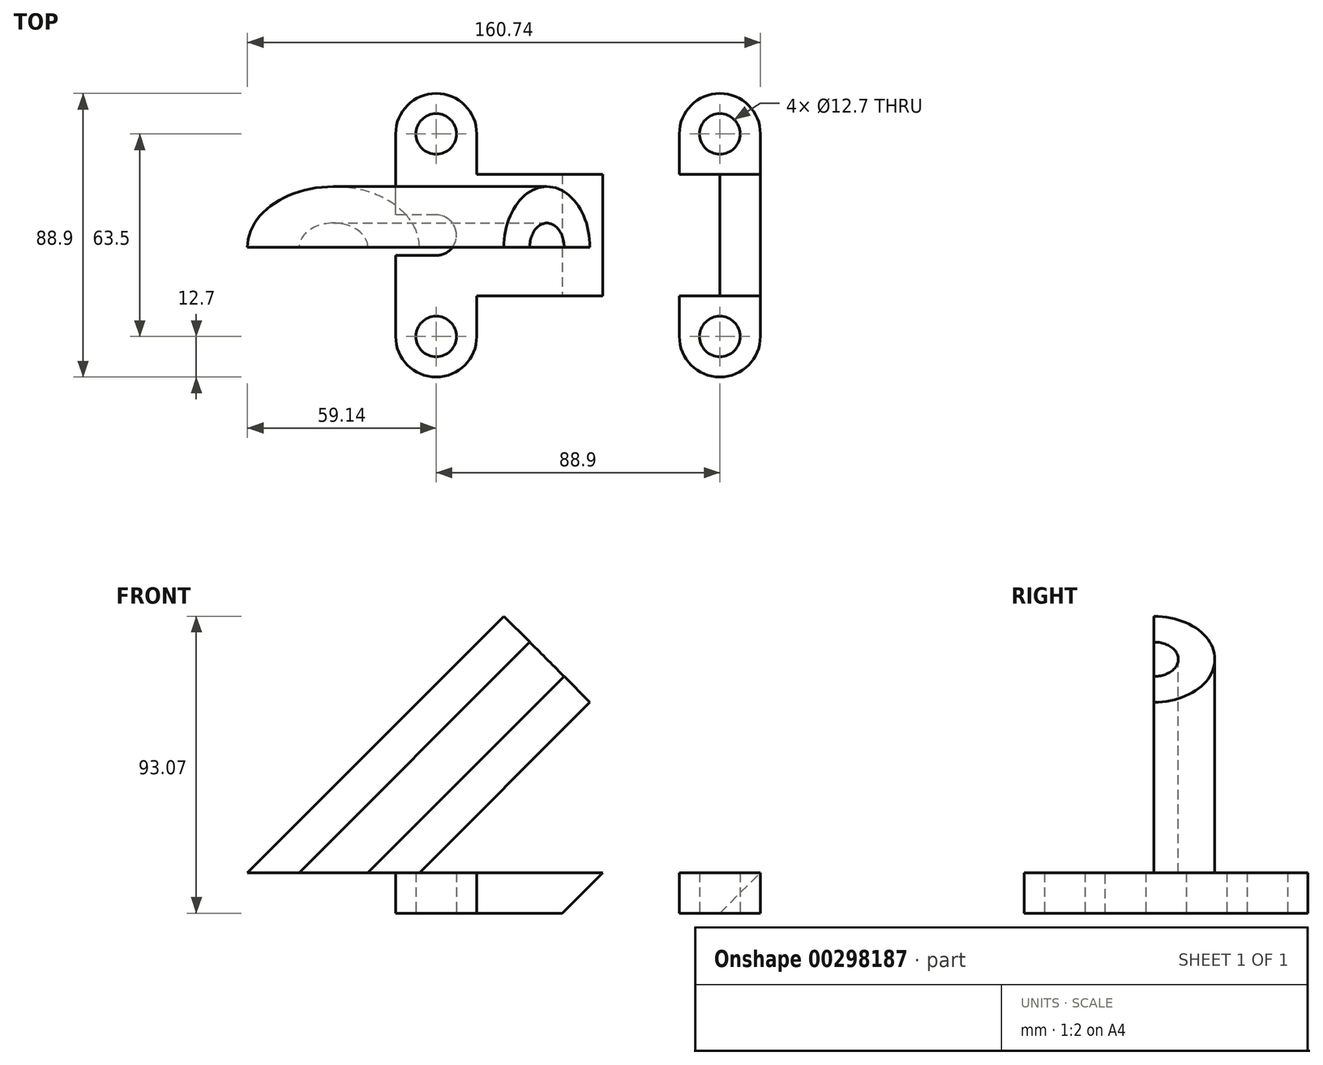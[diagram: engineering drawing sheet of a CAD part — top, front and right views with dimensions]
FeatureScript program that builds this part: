
annotation { "Feature Type Name" : "Feature", "Feature Type Description" : "" }
export const myFeature = defineFeature(function(context is Context, id is Id, definition is map)
    precondition{}
    {
        {
            var Q0;
            Q0=qCreatedBy(makeId("Top.planeOp"),FACE);
            var sketch = newSketch(context, id + "F0", { "sketchPlane" : qUnion([Q0])});
            skLineSegment(sketch, "E0", {"start": v(0, 0) * mm, "end": v(0, 63.5) * mm, "construction": true});
            skLineSegment(sketch, "E1", {"start": v(0, 63.5) * mm, "end": v(88.9, 63.5) * mm, "construction": true});
            skLineSegment(sketch, "E2", {"start": v(88.9, 63.5) * mm, "end": v(88.9, 0) * mm, "construction": true});
            skLineSegment(sketch, "E3", {"start": v(88.9, 0) * mm, "end": v(0, 0) * mm, "construction": true});
            skArc(sketch, "E4", {"start": v(12.7, 63.5) * mm, "mid": v(0, 76.2) * mm, "end": v(-12.7, 63.5) * mm});
            skArc(sketch, "E5", {"start": v(101.6, 63.5) * mm, "mid": v(88.9, 76.2) * mm, "end": v(76.2, 63.5) * mm});
            skArc(sketch, "E6", {"start": v(76.2, 0) * mm, "mid": v(88.9, -12.7) * mm, "end": v(101.6, 0) * mm});
            skArc(sketch, "E7", {"start": v(-12.7, 0) * mm, "mid": v(0, -12.7) * mm, "end": v(12.7, 0) * mm});
            skArc(sketch, "E8", {"start": v(0, 25.4) * mm, "mid": v(6.35, 31.75) * mm, "end": v(0, 38.1) * mm});
            skLineSegment(sketch, "E9", {"start": v(0, 31.75) * mm, "end": v(88.9, 31.75) * mm, "construction": true});
            skLineSegment(sketch, "E10", {"start": v(67.85, 31.75) * mm, "end": v(67.85, 50.8) * mm, "construction": true});
            skLineSegment(sketch, "E11", {"start": v(67.85, 31.75) * mm, "end": v(67.85, 12.7) * mm, "construction": true});
            skLineSegment(sketch, "E12", {"start": v(12.7, 63.5) * mm, "end": v(12.7, 50.8) * mm});
            skLineSegment(sketch, "E13", {"start": v(12.7, 50.8) * mm, "end": v(76.2, 50.8) * mm});
            skLineSegment(sketch, "E14", {"start": v(76.2, 50.8) * mm, "end": v(76.2, 63.5) * mm});
            skLineSegment(sketch, "E15", {"start": v(101.6, 63.5) * mm, "end": v(101.6, 0) * mm});
            skLineSegment(sketch, "E16", {"start": v(76.2, 0) * mm, "end": v(76.2, 12.7) * mm});
            skLineSegment(sketch, "E17", {"start": v(76.2, 12.7) * mm, "end": v(12.7, 12.7) * mm});
            skLineSegment(sketch, "E18", {"start": v(12.7, 12.7) * mm, "end": v(12.7, 0) * mm});
            skLineSegment(sketch, "E19", {"start": v(0, 38.1) * mm, "end": v(-12.7, 38.1) * mm});
            skLineSegment(sketch, "E20", {"start": v(-12.7, 38.1) * mm, "end": v(-12.7, 63.5) * mm});
            skLineSegment(sketch, "E21", {"start": v(0, 25.4) * mm, "end": v(-12.7, 25.4) * mm});
            skLineSegment(sketch, "E22", {"start": v(-12.7, 25.4) * mm, "end": v(-12.7, 0) * mm});
            skCircle(sketch, "E23", {"center": v(0, 63.5) * mm, "radius": 6.35 * mm});
            skCircle(sketch, "E24", {"center": v(88.9, 63.5) * mm, "radius": 6.35 * mm});
            skCircle(sketch, "E25", {"center": v(88.9, 0) * mm, "radius": 6.35 * mm});
            skCircle(sketch, "E26", {"center": v(0, 0) * mm, "radius": 6.35 * mm});
            skSolve(sketch);
        }
        {
            var Q0;
            Q0=makeQuery(id+"F0.imprint","IMPRINT",FACE,{"disambiguationData":[TD([[makeQuery(id+"F0.imprint","IMPRINT",EDGE,{"derivedFrom":sQuery(id+"F0.wireOp",EDGE,"E4")}),1.0]])]});
            extrude(context, id + "F1", {"entities" : qUnion([Q0]), "depth" : 12.7 * mm});
        }
        {
            var Q0;
            Q0=makeQuery(id+"F1.opExtrude","SWEPT_FACE",FACE,{"disambiguationData":[OSD([sQuery(id+"F0.wireOp",EDGE,"E17")])]});
            var sketch = newSketch(context, id + "F2", { "sketchPlane" : qUnion([Q0])});
            skLineSegment(sketch, "E27", {"start": v(101.6, 12.7) * mm, "end": v(76.9, 37.4) * mm});
            skLineSegment(sketch, "E28", {"start": v(76.9, 37.4) * mm, "end": v(52.2, 12.7) * mm});
            skLineSegment(sketch, "E29", {"start": v(52.2, 12.7) * mm, "end": v(101.6, 12.7) * mm});
            skSolve(sketch);
        }
        {
            var Q0;
            {var subQ0=sQuery(id+"F2.wireOp",EDGE,"E27");Q0=makeQuery(id+"F2.imprint","IMPRINT",FACE,{"disambiguationData":[TD([[makeQuery(id+"F2.imprint","IMPRINT",EDGE,{"derivedFrom":subQ0}),1.0]])]});}
            extrude(context, id + "F3", {"entities" : qUnion([Q0]), "operationType" : NewBodyOperationType.ADD, "oppositeDirection" : true, "depth" : 38.1 * mm});
        }
        {
            var Q0;
            Q0=makeQuery(id+"F3.opExtrude","SWEPT_FACE",FACE,{"disambiguationData":[OSD([sQuery(id+"F2.wireOp",EDGE,"E27")])]});
            var sketch = newSketch(context, id + "F4", { "sketchPlane" : qUnion([Q0])});
            skCircle(sketch, "E30", {"center": v(27.94, 31.75) * mm, "radius": 7.62 * mm});
            skCircle(sketch, "E31", {"center": v(27.94, 31.75) * mm, "radius": 19.05 * mm});
            skLineSegment(sketch, "E32", {"start": v(27.94, 12.7) * mm, "end": v(27.94, 50.8) * mm});
            skCircle(sketch, "E33", {"center": v(27.94, 31.75) * mm, "radius": 12.7 * mm, "construction": true});
            skSolve(sketch);
        }
        {
            var Q0;
            {var subQ0=sQuery(id+"F4.wireOp",EDGE,"E32");var subQ1=sQuery(id+"F4.wireOp",EDGE,"E30");var subQ2=makeQuery(id+"F4.imprint","INTERSECT",VERTEX,{"disambiguationData":[OD(0.0)],"derivedFrom":[subQ1,subQ0]});Q0=makeQuery(id+"F4.imprint","IMPRINT",FACE,{"disambiguationData":[TD([[makeQuery(id+"F4.imprint","IMPRINT",EDGE,{"disambiguationData":[TD([[subQ2,-1.0]])],"derivedFrom":subQ1}),-1.0]])]});}
            var Q1;
            {var subQ0=sQuery(id+"F0.wireOp",EDGE,"E20");var subQ1=sQuery(id+"F0.wireOp",EDGE,"E19");var subQ2=sQuery(id+"F0.wireOp",EDGE,"E18");var subQ3=sQuery(id+"F0.wireOp",EDGE,"E17");var subQ4=sQuery(id+"F0.wireOp",EDGE,"E13");var subQ5=sQuery(id+"F0.wireOp",EDGE,"E4");var subQ6=sQuery(id+"F0.wireOp",EDGE,"E21");var subQ7=sQuery(id+"F0.wireOp",EDGE,"E7");var subQ11=sQuery(id+"F0.wireOp",EDGE,"E8");var subQ12=sQuery(id+"F0.wireOp",EDGE,"E12");var subQ13=sQuery(id+"F0.wireOp",EDGE,"E22");var subQ14=sQuery(id+"F0.wireOp",EDGE,"E23");var subQ15=sQuery(id+"F0.wireOp",EDGE,"E26");Q1=makeQuery(id+"F3.boolean.opBoolean","SPLIT",FACE,{"disambiguationData":[TD([makeQuery(id+"F1.opExtrude","SWEPT_FACE",FACE,{"disambiguationData":[OSD([subQ5])]})])],"derivedFrom":makeQuery(id+"F1.opExtrude","CAP_FACE",FACE,{"disambiguationData":[OSD([subQ5,sQuery(id+"F0.wireOp",EDGE,"E5"),sQuery(id+"F0.wireOp",EDGE,"E6"),subQ7,subQ11,subQ12,subQ4,sQuery(id+"F0.wireOp",EDGE,"E14"),sQuery(id+"F0.wireOp",EDGE,"E15"),sQuery(id+"F0.wireOp",EDGE,"E16"),subQ3,subQ2,subQ1,subQ0,subQ6,subQ13,subQ14,sQuery(id+"F0.wireOp",EDGE,"E24"),sQuery(id+"F0.wireOp",EDGE,"E25"),subQ15])],"isStart":false})});}
            extrude(context, id + "F5", {"entities" : qUnion([Q0]), "operationType" : NewBodyOperationType.ADD, "endBound" : BoundingType.UP_TO_SURFACE, "oppositeDirection" : true, "endBoundEntityFace" : qUnion([Q1]), "depth" : 25 * mm});
        }
        {
            var Q0;
            Q0=makeQuery(id+"F5.boolean.opBoolean","MERGE",FACE,{"derivedFrom":[makeQuery(id+"F3.opExtrude","SWEPT_FACE",FACE,{"disambiguationData":[OSD([sQuery(id+"F2.wireOp",EDGE,"E27")])]}),makeQuery(id+"F5.opExtrude","CAP_FACE",FACE,{"disambiguationData":[OSD([sQuery(id+"F4.wireOp",EDGE,"E30"),sQuery(id+"F4.wireOp",EDGE,"E31"),sQuery(id+"F4.wireOp",EDGE,"E32")])],"isStart":true})]});
            var sketch = newSketch(context, id + "F6", { "sketchPlane" : qUnion([Q0])});
            skCircle(sketch, "E34", {"center": v(27.94, 31.75) * mm, "radius": 7.62 * mm});
            skSolve(sketch);
        }
        {
            var Q0;
            {var subQ1=makeQuery(id+"F3.opExtrude","SWEPT_EDGE",EDGE,{"disambiguationData":[OSD([sQuery(id+"F2.wireOp",EDGE,"E27"),sQuery(id+"F2.wireOp",EDGE,"E28")])]});Q0=makeQuery(id+"F6.imprint","IMPRINT",FACE,{"disambiguationData":[TD([[makeQuery(id+"F6.imprint","IMPRINT",EDGE,{"derivedFrom":subQ1}),1.0]])]});}
            var Q1;
            {var subQ1=makeQuery(id+"F3.opExtrude","SWEPT_EDGE",EDGE,{"disambiguationData":[OSD([sQuery(id+"F2.wireOp",EDGE,"E27"),sQuery(id+"F2.wireOp",EDGE,"E28")])]});Q1=makeQuery(id+"F6.imprint","IMPRINT",FACE,{"disambiguationData":[TD([[makeQuery(id+"F6.imprint","IMPRINT",EDGE,{"derivedFrom":subQ1}),-1.0]])]});}
            extrude(context, id + "F7", {"entities" : qUnion([Q0, Q1]), "operationType" : NewBodyOperationType.REMOVE, "endBound" : BoundingType.THROUGH_ALL, "oppositeDirection" : true, "depth" : 25 * mm});
        }
        {
            var Q0;
            Q0=makeQuery(id+"F5.boolean.opBoolean","MERGE",FACE,{"derivedFrom":[makeQuery(id+"F3.opExtrude","SWEPT_FACE",FACE,{"disambiguationData":[OSD([sQuery(id+"F2.wireOp",EDGE,"E27")])]}),makeQuery(id+"F5.opExtrude","CAP_FACE",FACE,{"disambiguationData":[OSD([sQuery(id+"F4.wireOp",EDGE,"E30"),sQuery(id+"F4.wireOp",EDGE,"E31"),sQuery(id+"F4.wireOp",EDGE,"E32")])],"isStart":true})]});
            var sketch = newSketch(context, id + "F8", { "sketchPlane" : qUnion([Q0])});
            skCircle(sketch, "E35", {"center": v(27.94, 31.75) * mm, "radius": 12.7 * mm, "construction": true});
            skCircle(sketch, "E36", {"center": v(15.24, 31.75) * mm, "radius": 2.54 * mm});
            skSolve(sketch);
        }
        {
            var Q0;
            Q0=makeQuery(id+"F8.imprint","IMPRINT",FACE,{"disambiguationData":[TD([[makeQuery(id+"F8.imprint","IMPRINT",EDGE,{"derivedFrom":sQuery(id+"F8.wireOp",EDGE,"E36")}),1.0]])]});
            extrude(context, id + "F9", {"entities" : qUnion([Q0]), "operationType" : NewBodyOperationType.REMOVE, "oppositeDirection" : true, "depth" : 6.35 * mm});
        }
    });
